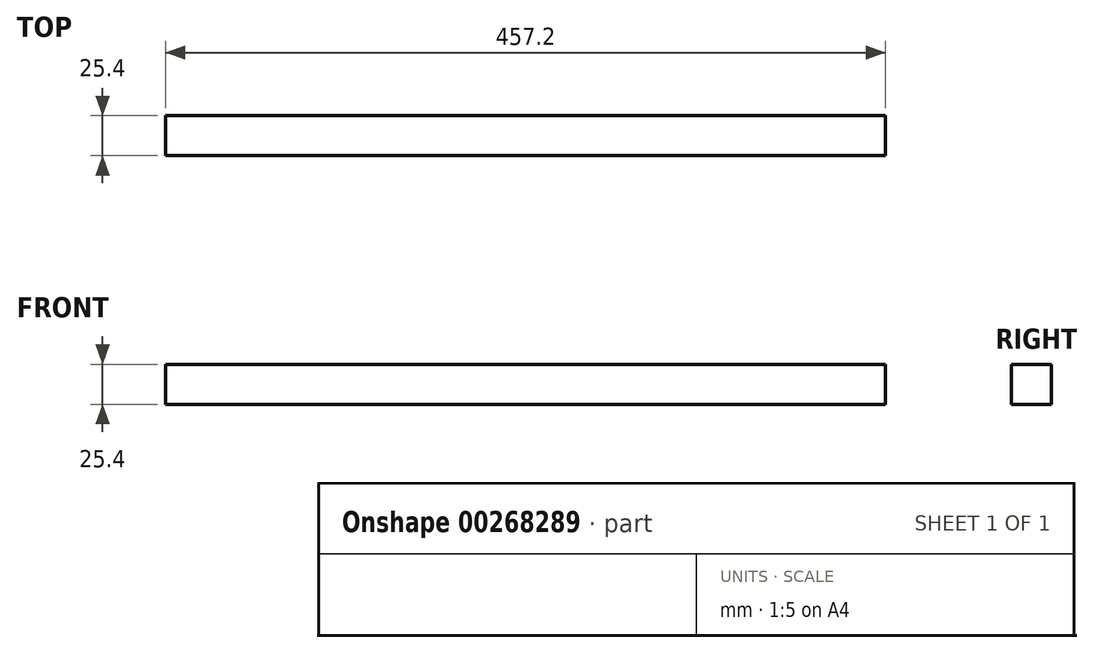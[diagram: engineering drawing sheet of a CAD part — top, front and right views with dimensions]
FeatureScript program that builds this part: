
annotation { "Feature Type Name" : "Feature", "Feature Type Description" : "" }
export const myFeature = defineFeature(function(context is Context, id is Id, definition is map)
    precondition{}
    {
        {
            var Q0;
            Q0=qCreatedBy(makeId("Front.planeOp"),FACE);
            var sketch = newSketch(context, id + "F0", { "sketchPlane" : qUnion([Q0])});
            skLineSegment(sketch, "E0.bottom", {"start": v(215.43, 34.11) * mm, "end": v(-241.77, 34.11) * mm});
            skLineSegment(sketch, "E0.top", {"start": v(215.43, 8.71) * mm, "end": v(-241.77, 8.71) * mm});
            skLineSegment(sketch, "E0.left", {"start": v(215.43, 34.11) * mm, "end": v(215.43, 8.71) * mm});
            skLineSegment(sketch, "E0.right", {"start": v(-241.77, 34.11) * mm, "end": v(-241.77, 8.71) * mm});
            skSolve(sketch);
        }
        {
            var Q0;
            Q0=makeQuery(id+"F0.imprint","IMPRINT",FACE,{"disambiguationData":[TD([[makeQuery(id+"F0.imprint","IMPRINT",EDGE,{"derivedFrom":sQuery(id+"F0.wireOp",EDGE,"E0.bottom")}),1.0]])]});
            extrude(context, id + "F1", {"entities" : qUnion([Q0]), "depth" : 25.4 * mm});
        }
    });
